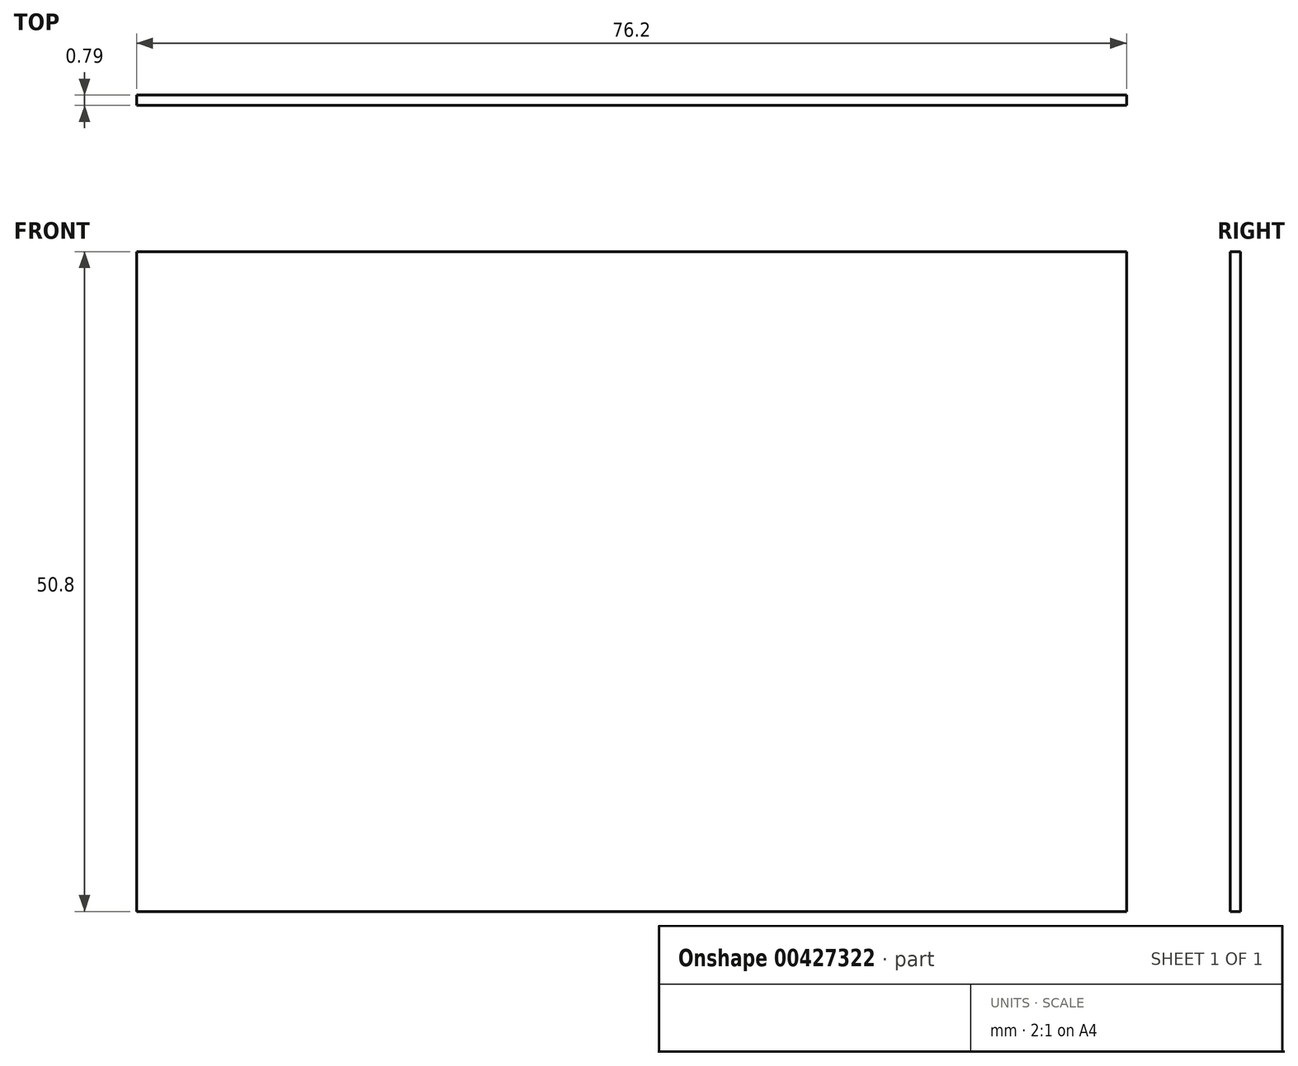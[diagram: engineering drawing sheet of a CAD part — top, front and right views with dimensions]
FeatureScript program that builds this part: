
annotation { "Feature Type Name" : "Feature", "Feature Type Description" : "" }
export const myFeature = defineFeature(function(context is Context, id is Id, definition is map)
    precondition{}
    {
        {
            var Q0;
            Q0=qCreatedBy(makeId("Front.planeOp"),FACE);
            var sketch = newSketch(context, id + "F0", { "sketchPlane" : qUnion([Q0])});
            skLineSegment(sketch, "E0.bottom", {"start": v(38.1, -25.4) * mm, "end": v(-38.1, -25.4) * mm});
            skLineSegment(sketch, "E0.top", {"start": v(38.1, 25.4) * mm, "end": v(-38.1, 25.4) * mm});
            skLineSegment(sketch, "E0.left", {"start": v(38.1, -25.4) * mm, "end": v(38.1, 25.4) * mm});
            skLineSegment(sketch, "E0.right", {"start": v(-38.1, -25.4) * mm, "end": v(-38.1, 25.4) * mm});
            skPoint(sketch, "E0.middle", {"position": v(0, 0) * mm});
            skSolve(sketch);
        }
        {
            var Q0;
            Q0 = qSketchRegion(id + "F0", true);
            extrude(context, id + "F1", {"entities" : qUnion([Q0]), "depth" : 0.8 * mm});
        }
    });
